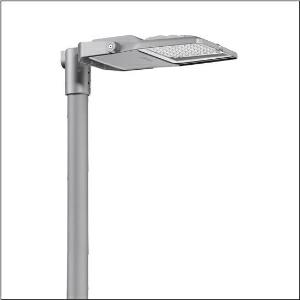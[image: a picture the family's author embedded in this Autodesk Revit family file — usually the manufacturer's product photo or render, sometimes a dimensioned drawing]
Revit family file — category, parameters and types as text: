
# Revit family: floodlight_fl_21_iq_mini___pl64_5xa7772d2e3a_5308
name_source: partatom
category: Lighting Fixtures
units: mm (PartAtom-declared; Revit-internal decimal feet)

## family parameters
Cut with Voids When Loaded = No
Host = Face
Light Source = No
Part Type = Normal
Room Calculation Point = No
Round Connector Dimension = Use Diameter
Shared = No

## types (1)
- --- (1 x LED, 17220 lm, 143 W, 3000K)
    Apparent Load = 143 VA
    CIE Flux Codes = 28 80 98 100 100
    Color Rendering = 70
    Color Temperature = 3000K
    Default Elevation = 1800 mm
    Description = Floodlight FL 21 iQ mini, floodlight, primary light control with lens, of PMMA, primary optical cover: protective disc, of toughened safety glass, transparent, light distribution: PL64, light emission: direct distribution, installation type: surface-mounted, LED, High Power LED, rated luminous flux: 17.220lm, luminous efficacy: 120lm/W, light colour: 730, colour temperature: 3000K, control: Auto-Match, Temp-Guard, Night-Set, Smart-Wire, Desk-Remote (wireless, voltage-free reading and setting of iQ features in the workshop via application-optimized NFC function/RFID function), optimised constant luminous flux control (CLO 2.0), Light-Fading, Lumen-Switch, with terminal, 6-pole, mains connection: 220..240V, AC, 50/60Hz, start of lifetime: 143W, end of service life: 152W, reduction: 61W, luminaire housing, of diecast aluminium, powder-coated, Siteco® metallic grey (DB 702S), corrosivity category C5 mid according to DIN EN ISO 12944, sealing non-destructively replaceable, please order mast flange separately, mast bracket, of steel, galvanised, powder-coated, protection rating (complete): IP66, insulation class (complete): insulation class II (safety insulation), certification: CE, ENEC, VDE, protection symbol: D, impact resistance: IK08, permissible operating ambient temperature: -40..+40°C, permissible operating ambient temperature for outdoor applications: -40..+50°C, standard: DIN EN 12944, LABS conformity tested according to VDMA 24364:2018-05, packaging unit: 1 piece

Light Distribution: PL64
    Height = 70 mm
    Lamp = 1 x LED
    Lamp Light Flux = 17220 lm
    Lamp Power = 143 W
    Lamp count = 1
    Length = 485 mm
    Luminous efficacy = 120 lm/W
    Manufacturer = Siteco
    ModVariant = No
    Model = 5XA7772D2E3A
    Number of Poles = 1
    OnlyDefault = Yes
    Power Factor = 1
    Product Name = Floodlight FL 21 iQ mini | PL64
    Product group = floodlight | pylon annexe
    ProductGroupID = 6200
    Protection Class = Protection class II
    Protection Degree = IP 66
    RLX_Detail_Level = 1
    RLX_Emergency_Light_Flux = 0 lm
    RLX_Emergency_Type = 0
    RLX_Emergency_Type_DB = No
    RlxData = <blob elided: 101557 chars, md5=bbfbfa78>
    Socket = socket
    Standby Power = 0 W
    System Light Flux = 17220 lm
    System Power = 143 W
    Type Comments = factory setting: luminous flux: 100 % | dim-lin: 254 | 730 mA
    Type Image = l_1007125.jpg
    URL = http://relux.com
    VarID = @adj_136135
    Voltage = 0 V
    Weight = 0.00 kg
    Width = 337 mm

## geometry (parser evidence)
native form markers: Blend x4, Sweep x12
no freeform markers — native parametric forms only
